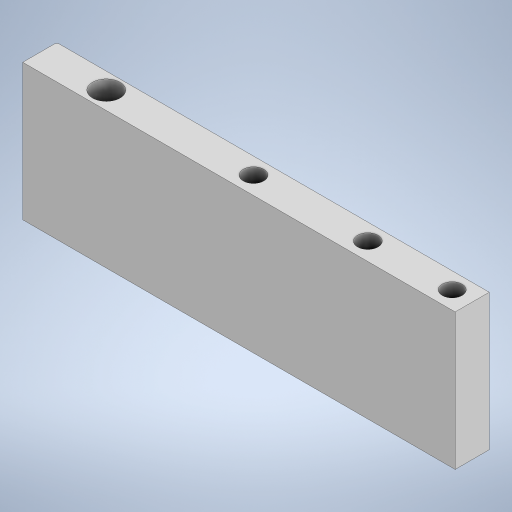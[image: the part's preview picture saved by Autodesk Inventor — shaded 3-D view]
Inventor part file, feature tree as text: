
AUTODESK INVENTOR PART (.ipt)
format: ipt  version: 2024 (Build 280153000, 153)  size: 217,600 bytes
history: native  units: in
note: dims shown in document units (in); Inventor stores cm internally (conversion verified against a paired STEP export)
features: sketch x3, extrude x2, fillet x1
ambient origin geometry x8: Origin, YZ Plane, XZ Plane, XY Plane, X Axis, Y Axis, Z Axis, Center Point
bodies: Solid1 (feature_tree)
feature tree (6):
  extrude  "Extrusion1"  Depth=0.9843in
  fillet  "Face Fillet1"
  extrude  "Extrusion4"  Depth=0.0787in
  sketch  "Sketch6"  dims[d16=0.5906in d17=0.5906in d18=3.937in d19=0.0in]
  sketch  "Sketch1"  dims[d0=12.4803in d1=0.9843in]
  sketch  "Sketch5"  dims[d2=3.937in d3=0.0in d15=0.0787in]
